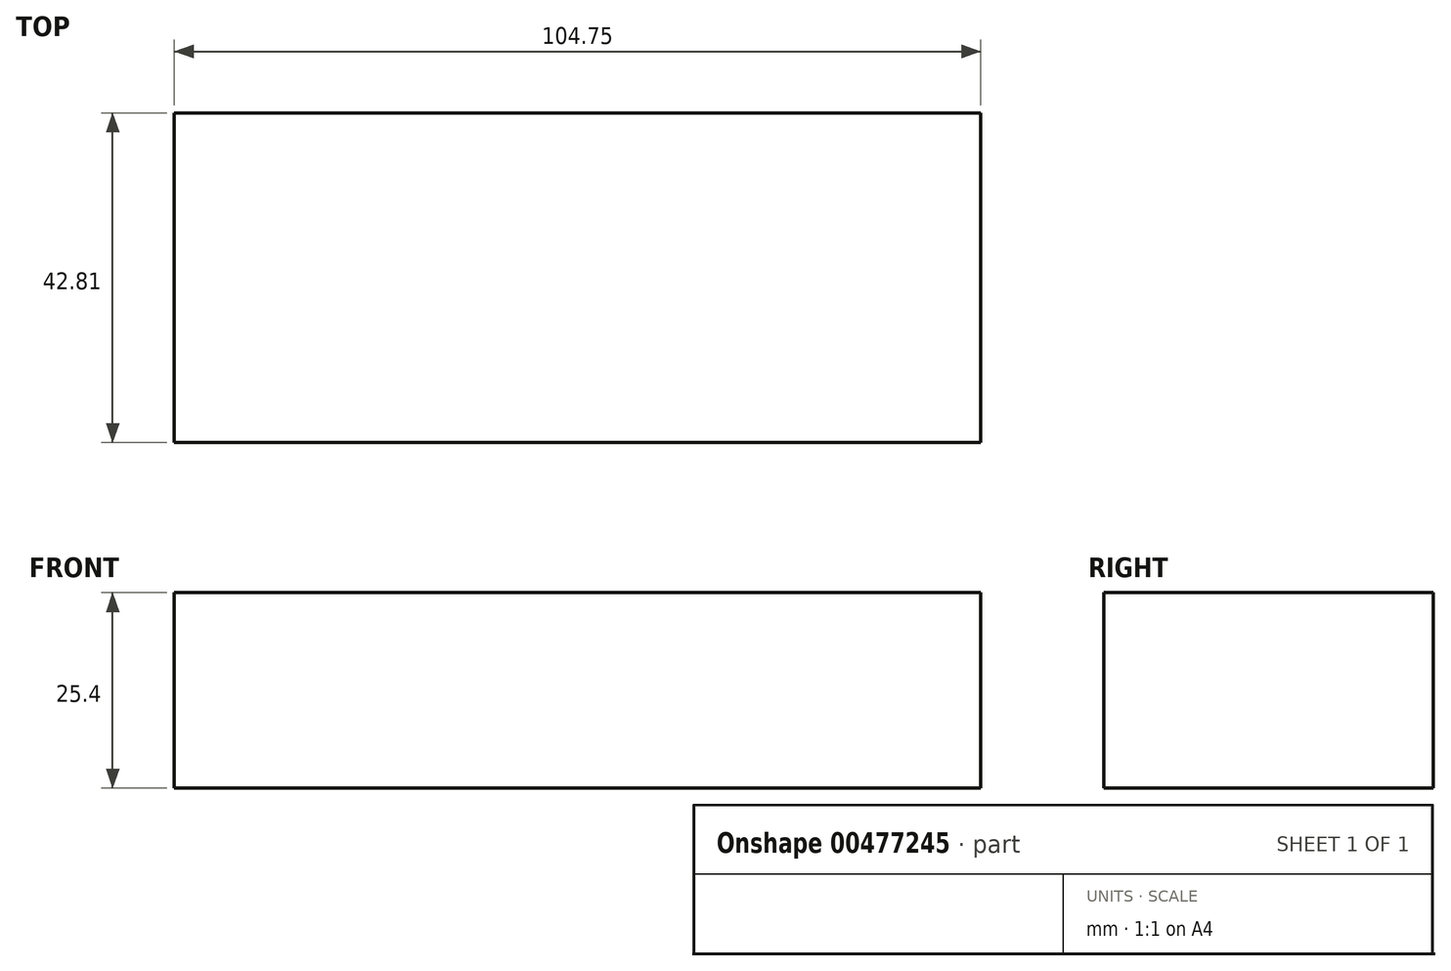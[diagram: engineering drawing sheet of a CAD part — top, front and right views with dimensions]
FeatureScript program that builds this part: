
annotation { "Feature Type Name" : "Feature", "Feature Type Description" : "" }
export const myFeature = defineFeature(function(context is Context, id is Id, definition is map)
    precondition{}
    {
        {
            var Q0;
            Q0=qCreatedBy(makeId("Top.planeOp"),FACE);
            var sketch = newSketch(context, id + "F0", { "sketchPlane" : qUnion([Q0])});
            skLineSegment(sketch, "E0.bottom", {"start": v(-59.3, 17.01) * mm, "end": v(45.45, 17.01) * mm});
            skLineSegment(sketch, "E0.top", {"start": v(-59.3, -25.8) * mm, "end": v(45.45, -25.8) * mm});
            skLineSegment(sketch, "E0.left", {"start": v(-59.3, 17.01) * mm, "end": v(-59.3, -25.8) * mm});
            skLineSegment(sketch, "E0.right", {"start": v(45.45, 17.01) * mm, "end": v(45.45, -25.8) * mm});
            skSolve(sketch);
        }
        {
            var Q0;
            Q0 = qSketchRegion(id + "F0", true);
            extrude(context, id + "F1", {"entities" : qUnion([Q0]), "depth" : 25.4 * mm});
        }
    });
